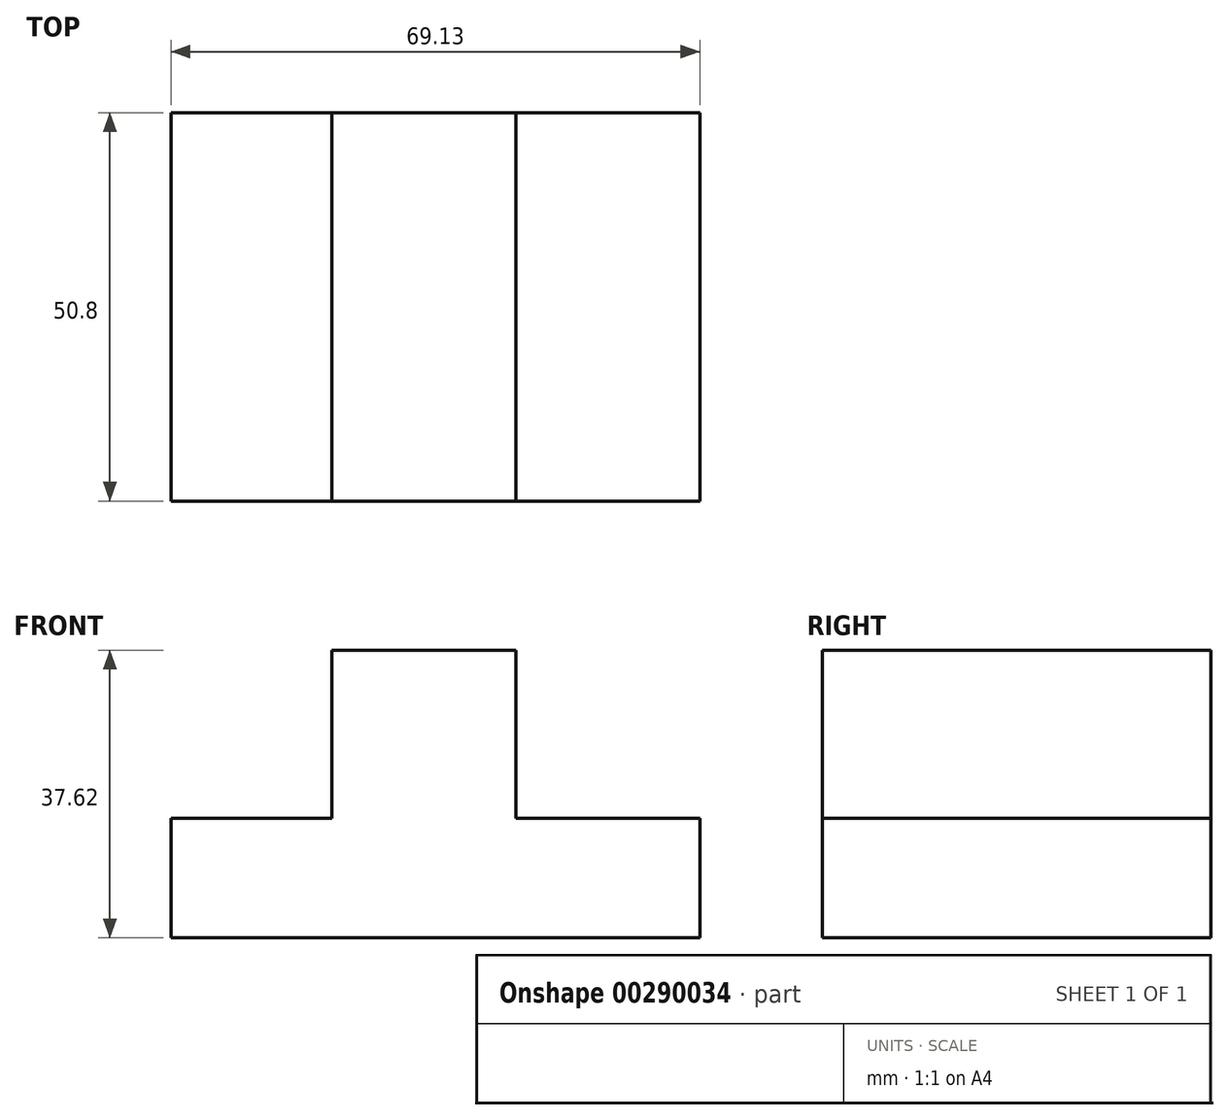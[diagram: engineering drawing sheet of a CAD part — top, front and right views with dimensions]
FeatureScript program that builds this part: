
annotation { "Feature Type Name" : "Feature", "Feature Type Description" : "" }
export const myFeature = defineFeature(function(context is Context, id is Id, definition is map)
    precondition{}
    {
        {
            var Q0;
            Q0=qCreatedBy(makeId("Front.planeOp"),FACE);
            var sketch = newSketch(context, id + "F0", { "sketchPlane" : qUnion([Q0])});
            skLineSegment(sketch, "E0.bottom", {"start": v(0, 0) * mm, "end": v(-69.13, 0) * mm});
            skLineSegment(sketch, "E0.top", {"start": v(0, 15.66) * mm, "end": v(-24.06, 15.66) * mm});
            skLineSegment(sketch, "E0.left", {"start": v(0, 0) * mm, "end": v(0, 15.66) * mm});
            skLineSegment(sketch, "E0.right", {"start": v(-69.13, 0) * mm, "end": v(-69.13, 15.66) * mm});
            skLineSegment(sketch, "E1.top", {"start": v(-48.12, 37.62) * mm, "end": v(-24.06, 37.62) * mm});
            skLineSegment(sketch, "E1.left", {"start": v(-48.12, 15.66) * mm, "end": v(-48.12, 37.62) * mm});
            skLineSegment(sketch, "E1.right", {"start": v(-24.06, 15.66) * mm, "end": v(-24.06, 37.62) * mm});
            skLineSegment(sketch, "E2.trimOffspring", {"start": v(-48.12, 15.66) * mm, "end": v(-69.13, 15.66) * mm});
            skSolve(sketch);
        }
        {
            var Q0;
            Q0=makeQuery(id+"F0.imprint","IMPRINT",FACE,{"disambiguationData":[TD([[makeQuery(id+"F0.imprint","IMPRINT",EDGE,{"derivedFrom":sQuery(id+"F0.wireOp",EDGE,"E0.bottom")}),-1.0]])]});
            extrude(context, id + "F1", {"entities" : qUnion([Q0]), "depth" : 50.8 * mm});
        }
    });
